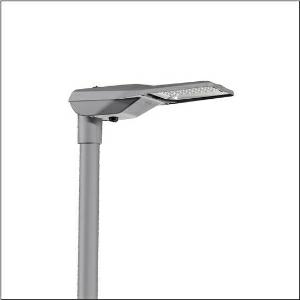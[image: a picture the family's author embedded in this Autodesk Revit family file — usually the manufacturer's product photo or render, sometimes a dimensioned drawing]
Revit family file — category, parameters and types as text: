
# Revit family: streetlight_sl_21_mini___st1_0a_5xe2d43t08gb_73de
name_source: partatom
category: Lighting Fixtures
units: mm (PartAtom-declared; Revit-internal decimal feet)

## family parameters
Cut with Voids When Loaded = No
Host = Face
Light Source = No
Part Type = Normal
Room Calculation Point = No
Round Connector Dimension = Use Diameter
Shared = No

## types (1)
- --- (1 x LED, 6180 lm, 40.4 W, 4000K)
    Apparent Load = 40 VA
    CIE Flux Codes = 37 72 97 100 100
    Color Rendering = 70
    Color Temperature = 4000K
    Default Elevation = 1800 mm
    Description = Streetlight SL 21 mini, mast luminaire, primary light control with lens, of PMMA, primary optical cover: cover, of toughened safety glass, transparent, light distribution: ST1.0a, light emission: direct distribution, primary light characteristic: asymmetric, installation type: side-entry, post-top, LED, High Power LED, rated luminous flux: 6.180lm, luminous efficacy: 153lm/W, light colour: 740, colour temperature: 4000K, control gear: D4i, control: overheat protection, constant luminous flux control, time-dependent luminous flux control, flexible luminous flux parameterisation, pre-setting: logarithmic dimming characteristic, mains connection: 220..240V, AC, 50/60Hz, start of lifetime: 40W, end of service life: 41W, reduction: 19W, luminaire housing, of diecast aluminium, powder-coated, Siteco® metallic grey (DB 702S), corrosivity category C5 mid according to DIN EN ISO 12944, please order mast flange separately, inclination adjustable: 0°, 5°, 10°, 15°, sealing non-destructively replaceable, multi-level sealing system, length: 628mm, width: 235mm, height: 110mm, mast flange for spigot size: 42mm (side-entry): 5XC10008XM4, 60/48mm (side-entry/post-top): 5XC10108XM2, 76/60mm (side-entry/post-top): 5XC10108XM1, mounting height: 4..8m, Smart Interface below and above, protection rating (complete): IP66, insulation class (complete): insulation class II (safety insulation), certification: CE, ENEC, ENEC+, VDE, impact resistance: IK10, permissible operating ambient temperature for outdoor applications: -40..+50°C, standard-compliant lighting for roads and squares, packaging unit: 1 piece

Light Distribution: ST1.0a
    Height = 110 mm
    Lamp = 1 x LED
    Lamp Light Flux = 6180 lm
    Lamp Power = 40.4 W
    Lamp count = 1
    Length = 625 mm
    Luminous efficacy = 153 lm/W
    Manufacturer = Siteco
    ModVariant = No
    Model = 5XE2D43T08GB
    Number of Poles = 1
    OnlyDefault = Yes
    Power Factor = 1
    Product Name = Streetlight SL 21 mini | ST1.0a
    Product group = mast luminaire | pylon top
    ProductGroupID = 6100
    Protection Class = Protection class II
    Protection Degree = IP 66
    RLX_Detail_Level = 1
    RLX_Emergency_Light_Flux = 0 lm
    RLX_Emergency_Type = 0
    RLX_Emergency_Type_DB = No
    RlxData = <blob elided: 26317 chars, md5=db1dcb03>
    Socket = socket
    Standby Power = 0 W
    System Light Flux = 6180 lm
    System Power = 40 W
    Type Comments = factory setting: luminous flux: 100 % | dim-lin: 254 | 812 mA
    Type Image = l_1003514.jpg
    URL = http://relux.com
    VarID = @adj_188542
    Voltage = 0 V
    Weight = 0.00 kg
    Width = 234 mm

## geometry (parser evidence)
native form markers: Blend x4, Sweep x9
no freeform markers — native parametric forms only
